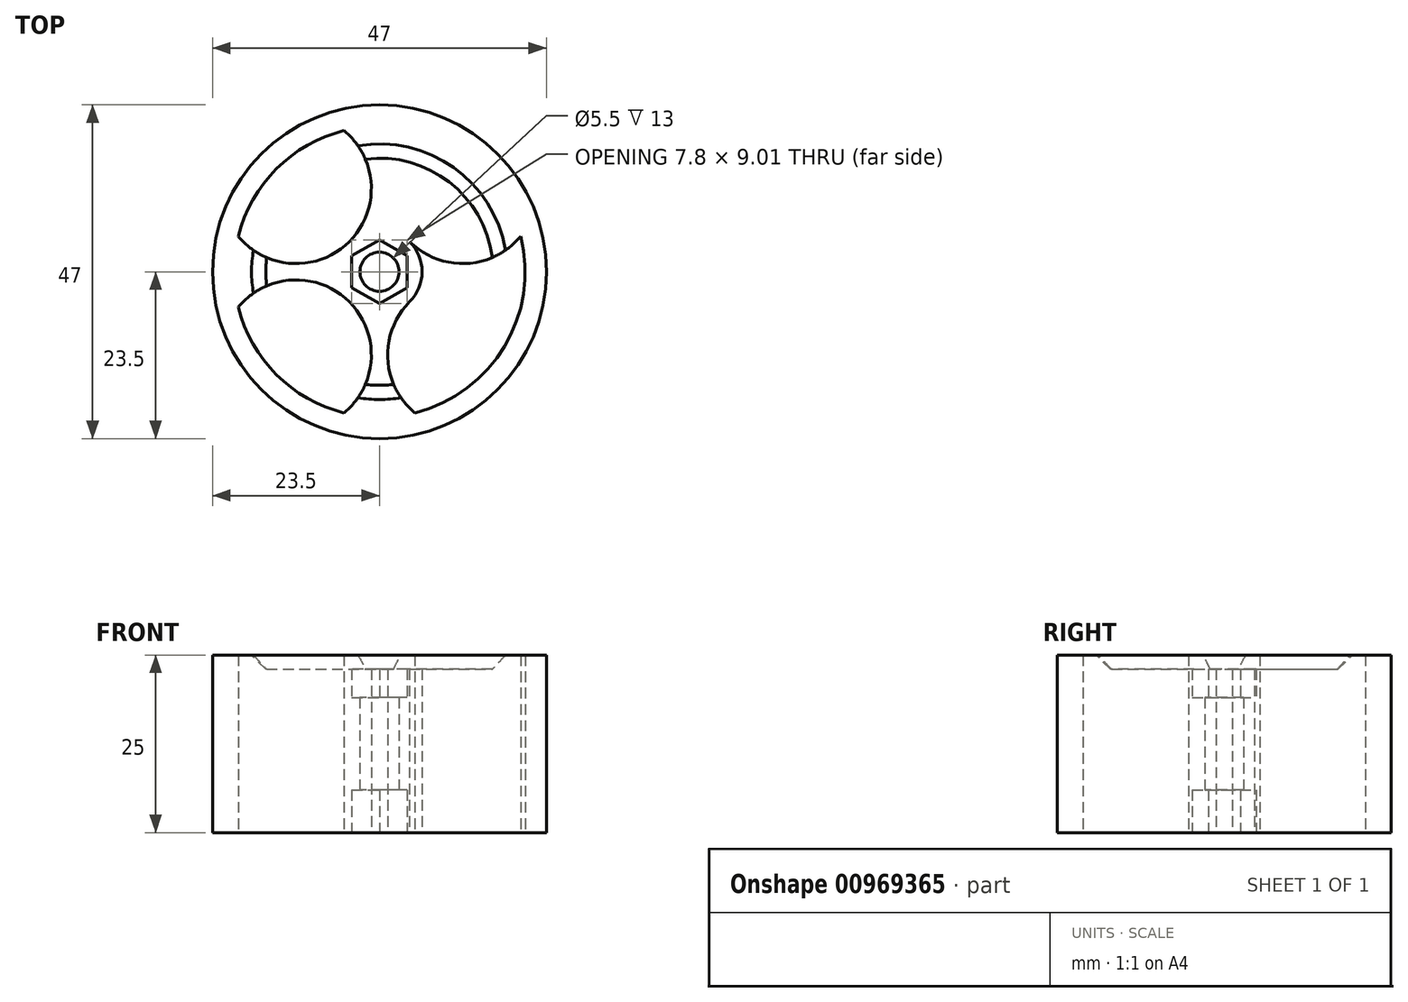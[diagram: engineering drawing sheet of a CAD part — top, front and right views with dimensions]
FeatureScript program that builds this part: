
annotation { "Feature Type Name" : "Feature", "Feature Type Description" : "" }
export const myFeature = defineFeature(function(context is Context, id is Id, definition is map)
    precondition{}
    {
        {
            var Q0;
            Q0=qCreatedBy(makeId("Top.planeOp"),FACE);
            var sketch = newSketch(context, id + "F0", { "sketchPlane" : qUnion([Q0])});
            skCircle(sketch, "E0", {"center": v(0, 0) * mm, "radius": 22.5 * mm});
            skCircle(sketch, "E1", {"center": v(0, 0) * mm, "radius": 20.5 * mm});
            skCircle(sketch, "E2", {"center": v(0, 0) * mm, "radius": 23.5 * mm});
            skCircle(sketch, "E3", {"center": v(0, 0) * mm, "radius": 6 * mm});
            skArc(sketch, "E4", {"start": v(-19.88, 5) * mm, "mid": v(-4.24, 4.24) * mm, "end": v(-5, 19.88) * mm});
            skArc(sketch, "E5.MirrorCS", {"start": v(19.88, 5) * mm, "mid": v(4.24, 4.24) * mm, "end": v(5, 19.88) * mm});
            skArc(sketch, "E6.MirrorCS", {"start": v(-19.88, -5) * mm, "mid": v(-4.24, -4.24) * mm, "end": v(-5, -19.88) * mm});
            skArc(sketch, "E7.MirrorCS", {"start": v(19.88, -5) * mm, "mid": v(4.24, -4.24) * mm, "end": v(5, -19.88) * mm});
            skCircle(sketch, "E8.cCircle", {"center": v(0, 0) * mm, "radius": 3.9 * mm, "construction": true});
            skLineSegment(sketch, "E8.0", {"start": v(-3.9, 2.25) * mm, "end": v(0, 4.5) * mm});
            skLineSegment(sketch, "E8.1", {"start": v(0, 4.5) * mm, "end": v(3.9, 2.25) * mm});
            skLineSegment(sketch, "E8.2", {"start": v(3.9, 2.25) * mm, "end": v(3.9, -2.25) * mm});
            skLineSegment(sketch, "E8.3", {"start": v(3.9, -2.25) * mm, "end": v(0, -4.5) * mm});
            skLineSegment(sketch, "E8.4", {"start": v(0, -4.5) * mm, "end": v(-3.9, -2.25) * mm});
            skLineSegment(sketch, "E8.5", {"start": v(-3.9, -2.25) * mm, "end": v(-3.9, 2.25) * mm});
            skPoint(sketch, "E8.0.midPoint", {"position": v(-1.95, 3.38) * mm});
            skCircle(sketch, "E9", {"center": v(0, 0) * mm, "radius": 2.75 * mm});
            skCircle(sketch, "E10", {"center": v(0, 0) * mm, "radius": 3 * mm});
            skSolve(sketch);
        }
        {
            var Q0;
            Q0=makeQuery(id+"F0.imprint","IMPRINT",FACE,{"disambiguationData":[TD([[makeQuery(id+"F0.imprint","IMPRINT",EDGE,{"derivedFrom":sQuery(id+"F0.wireOp",EDGE,"E0")}),1.0]])]});
            var Q1;
            Q1=makeQuery(id+"F0.imprint","IMPRINT",FACE,{"disambiguationData":[TD([[makeQuery(id+"F0.imprint","IMPRINT",EDGE,{"derivedFrom":sQuery(id+"F0.wireOp",EDGE,"E0")}),-1.0]])]});
            var Q2;
            {var subQ0=sQuery(id+"F0.wireOp",EDGE,"E4");var subQ1=sQuery(id+"F0.wireOp",EDGE,"E1");var subQ2=makeQuery(id+"F0.imprint","INTERSECT",VERTEX,{"disambiguationData":[OD(1.0)],"derivedFrom":[subQ1,subQ0]});Q2=makeQuery(id+"F0.imprint","IMPRINT",FACE,{"disambiguationData":[TD([[makeQuery(id+"F0.imprint","IMPRINT",EDGE,{"disambiguationData":[TD([[subQ2,1.0]])],"derivedFrom":subQ1}),1.0]])]});}
            var Q3;
            {var subQ0=sQuery(id+"F0.wireOp",EDGE,"E5.MirrorCS");var subQ1=sQuery(id+"F0.wireOp",EDGE,"E1");var subQ2=makeQuery(id+"F0.imprint","INTERSECT",VERTEX,{"disambiguationData":[OD(0.0)],"derivedFrom":[subQ1,subQ0]});Q3=makeQuery(id+"F0.imprint","IMPRINT",FACE,{"disambiguationData":[TD([[makeQuery(id+"F0.imprint","IMPRINT",EDGE,{"disambiguationData":[TD([[subQ2,1.0]])],"derivedFrom":subQ1}),1.0]])]});}
            var Q4;
            {var subQ0=sQuery(id+"F0.wireOp",EDGE,"E6.MirrorCS");var subQ1=sQuery(id+"F0.wireOp",EDGE,"E1");var subQ2=makeQuery(id+"F0.imprint","INTERSECT",VERTEX,{"disambiguationData":[OD(1.0)],"derivedFrom":[subQ1,subQ0]});Q4=makeQuery(id+"F0.imprint","IMPRINT",FACE,{"disambiguationData":[TD([[makeQuery(id+"F0.imprint","IMPRINT",EDGE,{"disambiguationData":[TD([[subQ2,-1.0]])],"derivedFrom":subQ1}),1.0]])]});}
            var Q5;
            {var subQ0=sQuery(id+"F0.wireOp",EDGE,"E4");var subQ1=sQuery(id+"F0.wireOp",EDGE,"E1");var subQ2=makeQuery(id+"F0.imprint","INTERSECT",VERTEX,{"disambiguationData":[OD(0.0)],"derivedFrom":[subQ1,subQ0]});Q5=makeQuery(id+"F0.imprint","IMPRINT",FACE,{"disambiguationData":[TD([[makeQuery(id+"F0.imprint","IMPRINT",EDGE,{"disambiguationData":[TD([[subQ2,-1.0]])],"derivedFrom":subQ1}),1.0]])]});}
            var Q6;
            Q6=makeQuery(id+"F0.imprint","IMPRINT",FACE,{"disambiguationData":[TD([[makeQuery(id+"F0.imprint","IMPRINT",EDGE,{"derivedFrom":sQuery(id+"F0.wireOp",EDGE,"E8.0")}),1.0]])]});
            var Q7;
            Q7=makeQuery(id+"F0.imprint","IMPRINT",FACE,{"disambiguationData":[TD([[makeQuery(id+"F0.imprint","IMPRINT",EDGE,{"derivedFrom":sQuery(id+"F0.wireOp",EDGE,"E8.0")}),-1.0]])]});
            extrude(context, id + "F1", {"entities" : qUnion([Q0, Q1, Q2, Q3, Q4, Q5, Q6, Q7]), "depth" : 25 * mm, "offsetDistance" : 25 * mm});
        }
        {
            var Q0;
            Q0=makeQuery(id+"F0.imprint","IMPRINT",FACE,{"disambiguationData":[TD([[makeQuery(id+"F0.imprint","IMPRINT",EDGE,{"derivedFrom":sQuery(id+"F0.wireOp",EDGE,"E9")}),-1.0]])]});
            extrude(context, id + "F2", {"entities" : qUnion([Q0]), "operationType" : NewBodyOperationType.ADD, "depth" : 23 * mm, "offsetDistance" : 25 * mm, "hasSecondDirection" : true, "secondDirectionOppositeDirection" : false, "secondDirectionDepth" : 2 * mm});
        }
        {
            var Q0;
            Q0=makeQuery(id+"F1.opExtrude","CAP_EDGE",EDGE,{"disambiguationData":[OSD([sQuery(id+"F0.wireOp",EDGE,"E10")])],"isStart":false});
            chamfer(context, id + "F3", {"entities" : qUnion([Q0]), "width" : 15 * mm, "tangentPropagation" : true});
        }
        {
            var Q0;
            Q0=makeQuery(id+"F0.imprint","IMPRINT",FACE,{"disambiguationData":[TD([[makeQuery(id+"F0.imprint","IMPRINT",EDGE,{"derivedFrom":sQuery(id+"F0.wireOp",EDGE,"E8.0")}),-1.0]])]});
            var Q1;
            Q1=makeQuery(id+"F2.opExtrude","CAP_FACE",FACE,{"disambiguationData":[OSD([sQuery(id+"F0.wireOp",EDGE,"E9"),sQuery(id+"F0.wireOp",EDGE,"E10")])],"isStart":false});
            var Q2;
            Q2=makeQuery(id+"F0.imprint","IMPRINT",FACE,{"disambiguationData":[TD([[makeQuery(id+"F0.imprint","IMPRINT",EDGE,{"derivedFrom":sQuery(id+"F0.wireOp",EDGE,"E9")}),-1.0]])]});
            extrude(context, id + "F4", {"entities" : qUnion([Q0, Q1, Q2]), "operationType" : NewBodyOperationType.REMOVE, "depth" : 6 * mm, "offsetDistance" : 25 * mm});
        }
        {
            var Q0;
            Q0=makeQuery(id+"F0.imprint","IMPRINT",FACE,{"disambiguationData":[TD([[makeQuery(id+"F0.imprint","IMPRINT",EDGE,{"derivedFrom":sQuery(id+"F0.wireOp",EDGE,"E8.0")}),-1.0]])]});
            var Q1;
            {var subQ0=sQuery(id+"F0.wireOp",EDGE,"E7.MirrorCS");var subQ1=sQuery(id+"F0.wireOp",EDGE,"E1");var subQ2=makeQuery(id+"F0.imprint","INTERSECT",VERTEX,{"disambiguationData":[OD(0.0)],"derivedFrom":[subQ1,subQ0]});Q1=makeQuery(id+"F0.imprint","IMPRINT",FACE,{"disambiguationData":[TD([[makeQuery(id+"F0.imprint","IMPRINT",EDGE,{"disambiguationData":[TD([[subQ2,1.0]])],"derivedFrom":subQ1}),1.0]])]});}
            var Q2;
            Q2=makeQuery(id+"F0.imprint","IMPRINT",FACE,{"disambiguationData":[TD([[makeQuery(id+"F0.imprint","IMPRINT",EDGE,{"derivedFrom":sQuery(id+"F0.wireOp",EDGE,"E9")}),-1.0]])]});
            extrude(context, id + "F5", {"entities" : qUnion([Q0, Q1, Q2]), "operationType" : NewBodyOperationType.REMOVE, "depth" : 25 * mm, "offsetDistance" : 25 * mm, "hasSecondDirection" : true, "secondDirectionOppositeDirection" : false, "secondDirectionDepth" : 19 * mm});
        }
    });
